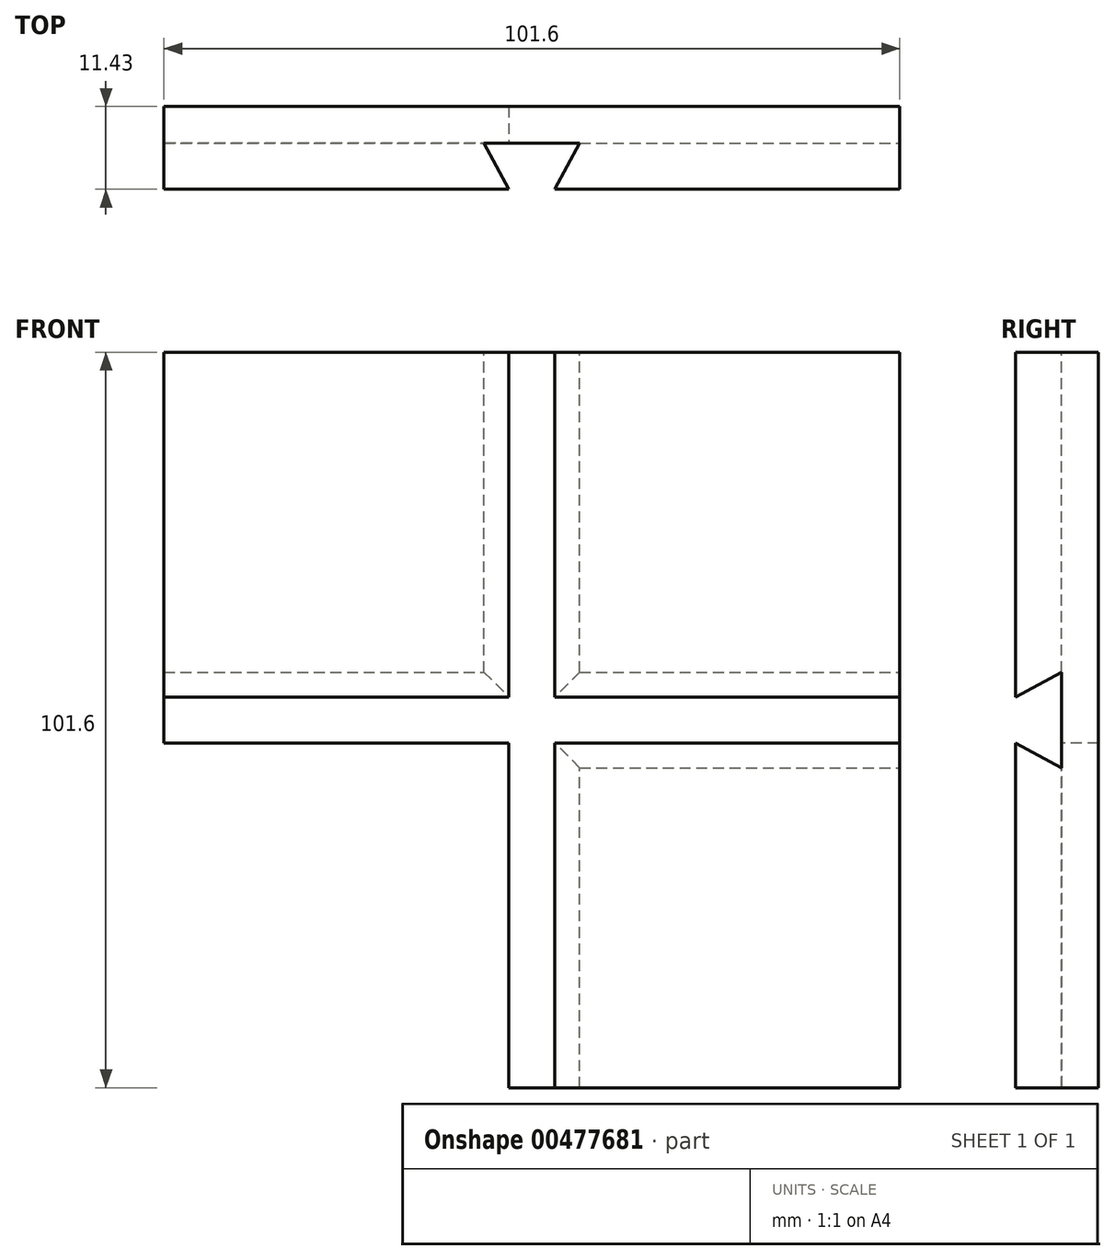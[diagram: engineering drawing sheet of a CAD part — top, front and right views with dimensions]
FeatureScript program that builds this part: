
annotation { "Feature Type Name" : "Feature", "Feature Type Description" : "" }
export const myFeature = defineFeature(function(context is Context, id is Id, definition is map)
    precondition{}
    {
        {
            var Q0;
            Q0=qCreatedBy(makeId("Front.planeOp"),FACE);
            var sketch = newSketch(context, id + "F0", { "sketchPlane" : qUnion([Q0])});
            skCircle(sketch, "E0", {"center": v(0, 0) * mm, "radius": 50.8 * mm});
            skCircle(sketch, "E1.cCircle", {"center": v(0, 0) * mm, "radius": 50.8 * mm, "construction": true});
            skLineSegment(sketch, "E1.0", {"start": v(-50.8, 50.8) * mm, "end": v(50.8, 50.8) * mm});
            skLineSegment(sketch, "E1.1", {"start": v(50.8, 50.8) * mm, "end": v(50.8, -50.8) * mm});
            skLineSegment(sketch, "E1.2", {"start": v(50.8, -50.8) * mm, "end": v(-50.8, -50.8) * mm});
            skLineSegment(sketch, "E1.3", {"start": v(-50.8, -50.8) * mm, "end": v(-50.8, 50.8) * mm});
            skPoint(sketch, "E1.0.midPoint", {"position": v(0, 50.8) * mm});
            skLineSegment(sketch, "E2.bottom", {"start": v(50.8, 3.17) * mm, "end": v(-50.8, 3.17) * mm});
            skLineSegment(sketch, "E2.top", {"start": v(50.8, -3.18) * mm, "end": v(-50.8, -3.18) * mm});
            skLineSegment(sketch, "E2.left", {"start": v(50.8, 3.18) * mm, "end": v(50.8, -3.18) * mm});
            skLineSegment(sketch, "E2.right", {"start": v(-50.8, 3.18) * mm, "end": v(-50.8, -3.18) * mm});
            skLineSegment(sketch, "E3.bottom", {"start": v(-3.18, 50.8) * mm, "end": v(3.18, 50.8) * mm});
            skLineSegment(sketch, "E3.top", {"start": v(-3.18, -50.8) * mm, "end": v(3.18, -50.8) * mm});
            skLineSegment(sketch, "E3.left", {"start": v(-3.18, 50.8) * mm, "end": v(-3.18, -50.8) * mm});
            skLineSegment(sketch, "E3.right", {"start": v(3.18, 50.8) * mm, "end": v(3.18, -50.8) * mm});
            skSolve(sketch);
        }
        {
            var Q0;
            Q0=qCreatedBy(makeId("Right.planeOp"),FACE);
            var sketch = newSketch(context, id + "F1", { "sketchPlane" : qUnion([Q0])});
            skLineSegment(sketch, "E4", {"start": v(7.44, 0) * mm, "end": v(0, 0) * mm, "construction": true});
            skLineSegment(sketch, "E5", {"start": v(0, 3.18) * mm, "end": v(6.35, 6.6) * mm});
            skLineSegment(sketch, "E6", {"start": v(6.35, 6.6) * mm, "end": v(6.35, 0) * mm});
            skLineSegment(sketch, "E7.MirrorCS", {"start": v(6.35, -6.6) * mm, "end": v(6.35, 0) * mm});
            skLineSegment(sketch, "E8.MirrorCS", {"start": v(0, -3.17) * mm, "end": v(6.35, -6.6) * mm});
            skLineSegment(sketch, "E9", {"start": v(0, 3.17) * mm, "end": v(0, -3.17) * mm});
            skSolve(sketch);
        }
        {
            var Q0;
            Q0=qCreatedBy(makeId("Top.planeOp"),FACE);
            var sketch = newSketch(context, id + "F2", { "sketchPlane" : qUnion([Q0])});
            skLineSegment(sketch, "E10", {"start": v(0, 0) * mm, "end": v(0, 3.3) * mm, "construction": true});
            skLineSegment(sketch, "E11", {"start": v(-3.17, 0) * mm, "end": v(-6.6, 6.35) * mm});
            skLineSegment(sketch, "E12", {"start": v(-6.6, 6.35) * mm, "end": v(0, 6.35) * mm});
            skLineSegment(sketch, "E13.MirrorCS", {"start": v(3.17, 0) * mm, "end": v(6.6, 6.35) * mm});
            skLineSegment(sketch, "E14.MirrorCS", {"start": v(6.6, 6.35) * mm, "end": v(0, 6.35) * mm});
            skLineSegment(sketch, "E15", {"start": v(-3.18, 0) * mm, "end": v(3.18, 0) * mm});
            skSolve(sketch);
        }
        {
            var Q0;
            {var subQ0=sQuery(id+"F0.wireOp",EDGE,"E2.left");var subQ1=sQuery(id+"F0.wireOp",EDGE,"E0");var subQ2=makeQuery(id+"F0.imprint","INTERSECT",VERTEX,{"derivedFrom":[subQ1,subQ0]});Q0=makeQuery(id+"F0.imprint","IMPRINT",FACE,{"disambiguationData":[TD([[makeQuery(id+"F0.imprint","IMPRINT",EDGE,{"disambiguationData":[TD([[subQ2,-1.0]])],"derivedFrom":subQ1}),-1.0]])]});}
            var Q1;
            {var subQ0=sQuery(id+"F0.wireOp",EDGE,"E3.bottom");var subQ1=sQuery(id+"F0.wireOp",EDGE,"E0");var subQ2=makeQuery(id+"F0.imprint","INTERSECT",VERTEX,{"derivedFrom":[subQ1,subQ0]});Q1=makeQuery(id+"F0.imprint","IMPRINT",FACE,{"disambiguationData":[TD([[makeQuery(id+"F0.imprint","IMPRINT",EDGE,{"disambiguationData":[TD([[subQ2,1.0]])],"derivedFrom":subQ1}),-1.0]])]});}
            var Q2;
            {var subQ0=sQuery(id+"F0.wireOp",EDGE,"E3.bottom");var subQ1=sQuery(id+"F0.wireOp",EDGE,"E0");var subQ2=makeQuery(id+"F0.imprint","INTERSECT",VERTEX,{"derivedFrom":[subQ1,subQ0]});Q2=makeQuery(id+"F0.imprint","IMPRINT",FACE,{"disambiguationData":[TD([[makeQuery(id+"F0.imprint","IMPRINT",EDGE,{"disambiguationData":[TD([[subQ2,-1.0]])],"derivedFrom":subQ1}),-1.0]])]});}
            var Q3;
            {var subQ0=sQuery(id+"F0.wireOp",EDGE,"E2.right");var subQ1=sQuery(id+"F0.wireOp",EDGE,"E0");var subQ2=makeQuery(id+"F0.imprint","INTERSECT",VERTEX,{"derivedFrom":[subQ1,subQ0]});Q3=makeQuery(id+"F0.imprint","IMPRINT",FACE,{"disambiguationData":[TD([[makeQuery(id+"F0.imprint","IMPRINT",EDGE,{"disambiguationData":[TD([[subQ2,1.0]])],"derivedFrom":subQ1}),-1.0]])]});}
            var Q4;
            {var subQ0=sQuery(id+"F0.wireOp",EDGE,"E2.right");var subQ1=sQuery(id+"F0.wireOp",EDGE,"E0");var subQ2=makeQuery(id+"F0.imprint","INTERSECT",VERTEX,{"derivedFrom":[subQ1,subQ0]});Q4=makeQuery(id+"F0.imprint","IMPRINT",FACE,{"disambiguationData":[TD([[makeQuery(id+"F0.imprint","IMPRINT",EDGE,{"disambiguationData":[TD([[subQ2,-1.0]])],"derivedFrom":subQ1}),-1.0]])]});}
            var Q5;
            {var subQ0=sQuery(id+"F0.wireOp",EDGE,"E3.top");var subQ1=sQuery(id+"F0.wireOp",EDGE,"E0");var subQ2=makeQuery(id+"F0.imprint","INTERSECT",VERTEX,{"derivedFrom":[subQ1,subQ0]});Q5=makeQuery(id+"F0.imprint","IMPRINT",FACE,{"disambiguationData":[TD([[makeQuery(id+"F0.imprint","IMPRINT",EDGE,{"disambiguationData":[TD([[subQ2,1.0]])],"derivedFrom":subQ1}),-1.0]])]});}
            var Q6;
            {var subQ0=sQuery(id+"F0.wireOp",EDGE,"E3.top");var subQ1=sQuery(id+"F0.wireOp",EDGE,"E0");var subQ2=makeQuery(id+"F0.imprint","INTERSECT",VERTEX,{"derivedFrom":[subQ1,subQ0]});Q6=makeQuery(id+"F0.imprint","IMPRINT",FACE,{"disambiguationData":[TD([[makeQuery(id+"F0.imprint","IMPRINT",EDGE,{"disambiguationData":[TD([[subQ2,-1.0]])],"derivedFrom":subQ1}),-1.0]])]});}
            var Q7;
            {var subQ0=sQuery(id+"F0.wireOp",EDGE,"E2.left");var subQ1=sQuery(id+"F0.wireOp",EDGE,"E0");var subQ2=makeQuery(id+"F0.imprint","INTERSECT",VERTEX,{"derivedFrom":[subQ1,subQ0]});Q7=makeQuery(id+"F0.imprint","IMPRINT",FACE,{"disambiguationData":[TD([[makeQuery(id+"F0.imprint","IMPRINT",EDGE,{"disambiguationData":[TD([[subQ2,1.0]])],"derivedFrom":subQ1}),-1.0]])]});}
            var Q8;
            {var subQ0=sQuery(id+"F0.wireOp",EDGE,"E2.bottom");var subQ3=sQuery(id+"F0.wireOp",EDGE,"E0");var subQ4=makeQuery(id+"F0.imprint","INTERSECT",VERTEX,{"disambiguationData":[OD(0.0)],"derivedFrom":[subQ3,subQ0]});Q8=makeQuery(id+"F0.imprint","IMPRINT",FACE,{"disambiguationData":[TD([[makeQuery(id+"F0.imprint","IMPRINT",EDGE,{"disambiguationData":[TD([[subQ4,-1.0]])],"derivedFrom":subQ3}),-1.0]])]});}
            var Q9;
            {var subQ3=sQuery(id+"F0.wireOp",EDGE,"E3.left");var subQ7=sQuery(id+"F0.wireOp",EDGE,"E0");var subQ9=makeQuery(id+"F0.imprint","INTERSECT",VERTEX,{"disambiguationData":[OD(0.0)],"derivedFrom":[subQ7,subQ3]});Q9=makeQuery(id+"F0.imprint","IMPRINT",FACE,{"disambiguationData":[TD([[makeQuery(id+"F0.imprint","IMPRINT",EDGE,{"disambiguationData":[TD([[subQ9,-1.0]])],"derivedFrom":subQ7}),-1.0]])]});}
            var Q10;
            {var subQ0=sQuery(id+"F0.wireOp",EDGE,"E2.top");var subQ3=sQuery(id+"F0.wireOp",EDGE,"E0");var subQ4=makeQuery(id+"F0.imprint","INTERSECT",VERTEX,{"disambiguationData":[OD(0.0)],"derivedFrom":[subQ3,subQ0]});Q10=makeQuery(id+"F0.imprint","IMPRINT",FACE,{"disambiguationData":[TD([[makeQuery(id+"F0.imprint","IMPRINT",EDGE,{"disambiguationData":[TD([[subQ4,-1.0]])],"derivedFrom":subQ3}),-1.0]])]});}
            var Q11;
            {var subQ3=sQuery(id+"F0.wireOp",EDGE,"E3.right");var subQ7=sQuery(id+"F0.wireOp",EDGE,"E0");var subQ9=makeQuery(id+"F0.imprint","INTERSECT",VERTEX,{"disambiguationData":[OD(1.0)],"derivedFrom":[subQ7,subQ3]});Q11=makeQuery(id+"F0.imprint","IMPRINT",FACE,{"disambiguationData":[TD([[makeQuery(id+"F0.imprint","IMPRINT",EDGE,{"disambiguationData":[TD([[subQ9,-1.0]])],"derivedFrom":subQ7}),-1.0]])]});}
            var Q12;
            {var subQ1=sQuery(id+"F0.wireOp",EDGE,"E0");var subQ8=makeQuery(id+"F0.imprint","INTERSECT",VERTEX,{"derivedFrom":[subQ1,sQuery(id+"F0.wireOp",EDGE,"E2.left")]});Q12=makeQuery(id+"F0.imprint","IMPRINT",FACE,{"disambiguationData":[TD([[makeQuery(id+"F0.imprint","IMPRINT",EDGE,{"disambiguationData":[TD([[subQ8,-1.0]])],"derivedFrom":subQ1}),1.0]])]});}
            var Q13;
            {var subQ1=sQuery(id+"F0.wireOp",EDGE,"E0");var subQ5=makeQuery(id+"F0.imprint","INTERSECT",VERTEX,{"derivedFrom":[subQ1,sQuery(id+"F0.wireOp",EDGE,"E3.bottom")]});Q13=makeQuery(id+"F0.imprint","IMPRINT",FACE,{"disambiguationData":[TD([[makeQuery(id+"F0.imprint","IMPRINT",EDGE,{"disambiguationData":[TD([[subQ5,1.0]])],"derivedFrom":subQ1}),1.0]])]});}
            var Q14;
            {var subQ1=sQuery(id+"F0.wireOp",EDGE,"E0");var subQ5=makeQuery(id+"F0.imprint","INTERSECT",VERTEX,{"derivedFrom":[subQ1,sQuery(id+"F0.wireOp",EDGE,"E2.right")]});Q14=makeQuery(id+"F0.imprint","IMPRINT",FACE,{"disambiguationData":[TD([[makeQuery(id+"F0.imprint","IMPRINT",EDGE,{"disambiguationData":[TD([[subQ5,1.0]])],"derivedFrom":subQ1}),1.0]])]});}
            var Q15;
            {var subQ1=sQuery(id+"F0.wireOp",EDGE,"E0");var subQ5=makeQuery(id+"F0.imprint","INTERSECT",VERTEX,{"derivedFrom":[subQ1,sQuery(id+"F0.wireOp",EDGE,"E3.top")]});Q15=makeQuery(id+"F0.imprint","IMPRINT",FACE,{"disambiguationData":[TD([[makeQuery(id+"F0.imprint","IMPRINT",EDGE,{"disambiguationData":[TD([[subQ5,1.0]])],"derivedFrom":subQ1}),1.0]])]});}
            var Q16;
            {var subQ0=sQuery(id+"F0.wireOp",EDGE,"E2.bottom");var subQ1=sQuery(id+"F0.wireOp",EDGE,"E0");var subQ2=makeQuery(id+"F0.imprint","INTERSECT",VERTEX,{"disambiguationData":[OD(0.0)],"derivedFrom":[subQ1,subQ0]});Q16=makeQuery(id+"F0.imprint","IMPRINT",FACE,{"disambiguationData":[TD([[makeQuery(id+"F0.imprint","IMPRINT",EDGE,{"disambiguationData":[TD([[subQ2,-1.0]])],"derivedFrom":subQ1}),1.0]])]});}
            var Q17;
            {var subQ0=sQuery(id+"F0.wireOp",EDGE,"E3.left");var subQ1=sQuery(id+"F0.wireOp",EDGE,"E0");var subQ2=makeQuery(id+"F0.imprint","INTERSECT",VERTEX,{"disambiguationData":[OD(0.0)],"derivedFrom":[subQ1,subQ0]});Q17=makeQuery(id+"F0.imprint","IMPRINT",FACE,{"disambiguationData":[TD([[makeQuery(id+"F0.imprint","IMPRINT",EDGE,{"disambiguationData":[TD([[subQ2,-1.0]])],"derivedFrom":subQ1}),1.0]])]});}
            var Q18;
            {var subQ0=sQuery(id+"F0.wireOp",EDGE,"E3.right");var subQ1=sQuery(id+"F0.wireOp",EDGE,"E0");var subQ2=makeQuery(id+"F0.imprint","INTERSECT",VERTEX,{"disambiguationData":[OD(1.0)],"derivedFrom":[subQ1,subQ0]});Q18=makeQuery(id+"F0.imprint","IMPRINT",FACE,{"disambiguationData":[TD([[makeQuery(id+"F0.imprint","IMPRINT",EDGE,{"disambiguationData":[TD([[subQ2,-1.0]])],"derivedFrom":subQ1}),1.0]])]});}
            var Q19;
            {var subQ0=sQuery(id+"F0.wireOp",EDGE,"E2.top");var subQ1=sQuery(id+"F0.wireOp",EDGE,"E0");var subQ2=makeQuery(id+"F0.imprint","INTERSECT",VERTEX,{"disambiguationData":[OD(0.0)],"derivedFrom":[subQ1,subQ0]});Q19=makeQuery(id+"F0.imprint","IMPRINT",FACE,{"disambiguationData":[TD([[makeQuery(id+"F0.imprint","IMPRINT",EDGE,{"disambiguationData":[TD([[subQ2,-1.0]])],"derivedFrom":subQ1}),1.0]])]});}
            var Q20;
            {var subQ0=sQuery(id+"F0.wireOp",EDGE,"E3.right");var subQ1=sQuery(id+"F0.wireOp",EDGE,"E2.bottom");var subQ2=makeQuery(id+"F0.imprint","INTERSECT",VERTEX,{"derivedFrom":[subQ1,subQ0]});Q20=makeQuery(id+"F0.imprint","IMPRINT",FACE,{"disambiguationData":[TD([[makeQuery(id+"F0.imprint","IMPRINT",EDGE,{"disambiguationData":[TD([[subQ2,-1.0]])],"derivedFrom":subQ1}),1.0]])]});}
            extrude(context, id + "F3", {"entities" : qUnion([Q0, Q1, Q2, Q3, Q4, Q5, Q6, Q7, Q8, Q9, Q10, Q11, Q12, Q13, Q14, Q15, Q16, Q17, Q18, Q19, Q20]), "oppositeDirection" : true, "depth" : 11.43 * mm, "offsetDistance" : 25.4 * mm});
        }
        {
            var Q0;
            Q0 = qSketchRegion(id + "F1", true);
            extrude(context, id + "F4", {"entities" : qUnion([Q0]), "operationType" : NewBodyOperationType.REMOVE, "endBound" : BoundingType.SYMMETRIC, "oppositeDirection" : true, "depth" : 101.6 * mm, "offsetDistance" : 25.4 * mm});
        }
        {
            var Q0;
            Q0 = qSketchRegion(id + "F2", true);
            extrude(context, id + "F5", {"entities" : qUnion([Q0]), "operationType" : NewBodyOperationType.REMOVE, "endBound" : BoundingType.SYMMETRIC, "oppositeDirection" : true, "depth" : 101.6 * mm, "offsetDistance" : 25.4 * mm});
        }
    });
